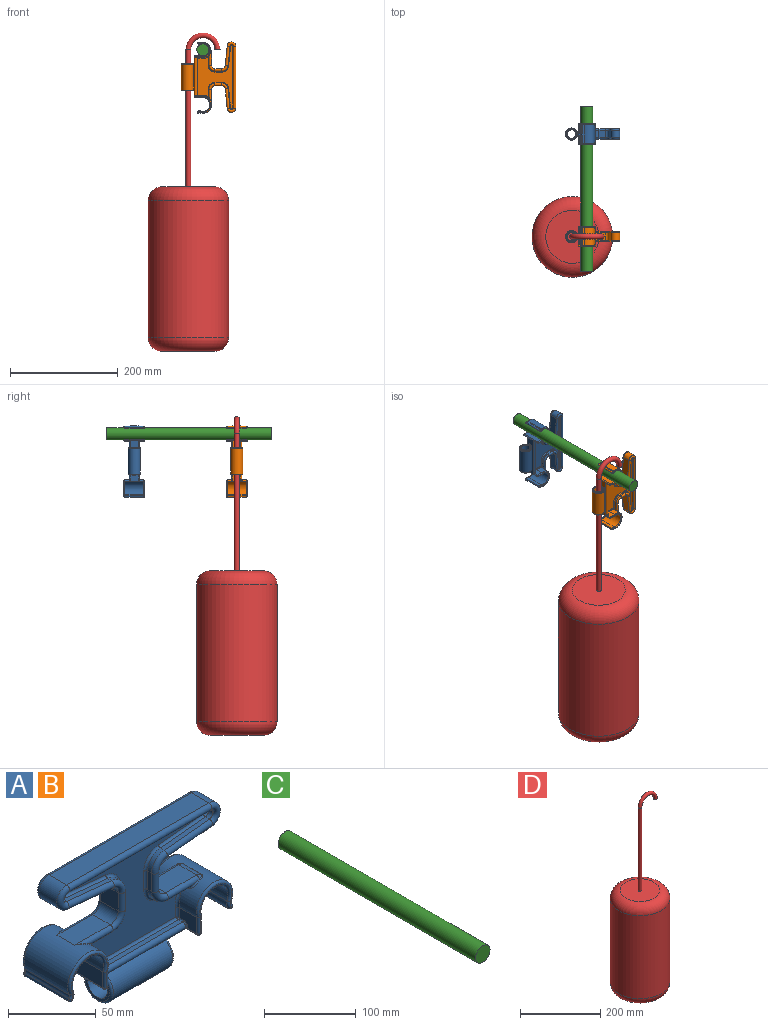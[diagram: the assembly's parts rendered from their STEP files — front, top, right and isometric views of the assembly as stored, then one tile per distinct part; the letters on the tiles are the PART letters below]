
ASSEMBLY  parts=4 mates=3
PART A: 234 faces, bbox 134.5x38.1x102.4 mm
  f0: plane 117.86x64.39mm, normal (0,-1,0), area 2891.2mm2, adj f101,f102,f103,f104,f105,f106,f107,f108
  f1: plane 117.86x64.39mm, normal (0,1,0), area 2891.2mm2, adj f165,f166,f167,f168,f169,f170,f171,f172
  f2: plane 70.47x3.18mm, normal (0,0,1), area 223.7mm2, adj f99,f179,f197,f205
  f3: plane 21.46x19.43mm, normal (1,0,0), area 103.6mm2, adj f69,f219,f228,f229,f230,f231,f232
  f4: plane 21.46x19.43mm, normal (-1,0,0), area 103.6mm2, adj f69,f216,f221,f222,f223,f224,f225
  f5: plane 47.75x0.17mm, normal (0,-1,0), area 8.3mm2, adj f214,f217,f225,f232
  f6: plane 47.75x0.17mm, normal (0,1,0), area 8.3mm2, adj f215,f218,f221,f228
  f7: plane 75.55x35.05mm, normal (0,0,-1), area 753mm2, adj f99,f100,f122,f127,f133,f138,f141,f147
  f8: plane 70.47x3.18mm, normal (0,0,1), area 223.7mm2, adj f100,f112,f201,f211
  f9: plane 17.54x3.18mm, normal (0,0,-1), area 55.7mm2, adj f17,f83,f106,f193
  f10: plane 12.7x3.18mm, normal (-1,0,0), area 40.3mm2, adj f16,f17,f81,f102
  f11: plane 36.31x3.5mm, normal (-0.1,0,1), area 115.8mm2, adj f16,f21,f79,f103
  f12: plane 114.3x3.18mm, normal (0,0,-1), area 362.9mm2, adj f44,f46,f92,f168
  f13: plane 36.31x3.5mm, normal (0.1,0,1), area 115.8mm2, adj f19,f20,f75,f111
  f14: plane 12.7x3.18mm, normal (1,0,0), area 40.3mm2, adj f18,f19,f73,f115
  f15: plane 15.44x3.18mm, normal (0,0,-1), area 49mm2, adj f18,f71,f118,f184
  f16: cylinder r=11.18mm len=11.12mm, axis (0,1,0), area 52.3mm2, adj f10,f11,f80,f101
  f17: cylinder r=11.18mm len=11.18mm, axis (0,1,0), area 55.7mm2, adj f9,f10,f82,f104
  f18: cylinder r=11.18mm len=11.18mm, axis (0,1,0), area 55.7mm2, adj f14,f15,f72,f117
  f19: cylinder r=11.18mm len=11.12mm, axis (0,1,0), area 52.3mm2, adj f13,f14,f74,f113
  f20: cylinder r=3.3mm len=6.59mm, axis (0,1,0), area 31.9mm2, adj f13,f45,f76,f109
  f21: cylinder r=3.3mm len=6.59mm, axis (0,1,0), area 31.9mm2, adj f11,f45,f78,f105
  f22: cylinder r=11.18mm len=11.12mm, axis (0,1,0), area 52.3mm2, adj f23,f47,f89,f174
  f23: plane 12.7x3.18mm, normal (-1,0,0), area 40.3mm2, adj f22,f24,f88,f176
  f24: cylinder r=11.18mm len=11.18mm, axis (0,1,0), area 55.7mm2, adj f23,f25,f87,f178
  f25: plane 17.54x3.18mm, normal (0,0,-1), area 55.7mm2, adj f24,f85,f180,f187
  f26: plane 24.89x14.22mm, normal (0,0,1), area 354mm2, adj f27,f70,f83,f85
  f27: cylinder r=6.35mm len=14.22mm, axis (0,1,0), area 141.9mm2, adj f26,f28,f82,f87
  f28: plane 14.22x12.7mm, normal (1,0,0), area 180.6mm2, adj f27,f29,f81,f88
  f29: cylinder r=6.35mm len=14.22mm, axis (0,1,0), area 133.2mm2, adj f28,f30,f80,f89
  f30: plane 36.31x14.22mm, normal (0.1,0,-1), area 518.9mm2, adj f29,f31,f79,f90
  f31: cylinder r=8.13mm len=16.22mm, axis (0,1,0), area 352.1mm2, adj f30,f32,f78,f91
  f32: plane 114.3x14.22mm, normal (0,0,1), area 1625.8mm2, adj f31,f33,f77,f92
  f33: cylinder r=8.13mm len=16.22mm, axis (0,1,0), area 352.1mm2, adj f32,f34,f76,f93
  f34: plane 36.31x14.22mm, normal (-0.1,0,-1), area 518.9mm2, adj f33,f35,f75,f94
  f35: cylinder r=6.35mm len=14.22mm, axis (0,1,0), area 133.2mm2, adj f34,f36,f74,f95
  f36: plane 14.22x12.7mm, normal (-1,0,0), area 180.6mm2, adj f35,f37,f73,f96
  f37: cylinder r=6.35mm len=14.22mm, axis (0,1,0), area 141.9mm2, adj f36,f38,f72,f97
  f38: plane 28.58x14.22mm, normal (0,0,1), area 406.5mm2, adj f37,f50,f71,f98
  f39: plane 15.44x3.18mm, normal (0,0,-1), area 49mm2, adj f40,f98,f173,f208
  f40: cylinder r=11.18mm len=11.18mm, axis (0,1,0), area 55.7mm2, adj f39,f41,f97,f171
  f41: plane 12.7x3.18mm, normal (1,0,0), area 40.3mm2, adj f40,f42,f96,f169
  f42: cylinder r=11.18mm len=11.12mm, axis (0,1,0), area 52.3mm2, adj f41,f43,f95,f167
  f43: plane 36.31x3.5mm, normal (0.1,0,1), area 115.8mm2, adj f42,f44,f94,f165
  f44: cylinder r=3.3mm len=6.59mm, axis (0,1,0), area 31.9mm2, adj f12,f43,f93,f166
  f45: plane 114.3x3.18mm, normal (0,0,-1), area 362.9mm2, adj f20,f21,f77,f107
  f46: cylinder r=3.3mm len=6.59mm, axis (0,1,0), area 31.9mm2, adj f12,f47,f91,f170
  f47: plane 36.31x3.5mm, normal (-0.1,0,1), area 115.8mm2, adj f22,f46,f90,f172
  f48: plane 13.59x10.78mm, normal (1,0,0), area 122.9mm2, adj f50,f114,f146,f147,f211,f212
  f49: plane 13.59x10.78mm, normal (1,0,0), area 122.9mm2, adj f50,f161,f164,f177,f204,f205
  f50: cylinder r=16mm len=35.05mm, axis (0,1,0), area 1712.8mm2, adj f38,f48,f49,f51,f116,f144,f159,f175
  f51: cylinder r=3.05mm len=35.05mm, axis (0,1,0), area 100.7mm2, adj f50,f52,f142,f156
  f52: cylinder r=1.65mm len=35.05mm, axis (0,1,0), area 181.8mm2, adj f51,f53,f143,f153
  f53: cylinder r=6.35mm len=35.05mm, axis (0,1,0), area 209.8mm2, adj f52,f54,f145,f150
  f54: cylinder r=12.7mm len=35.05mm, axis (0,1,0), area 1670.4mm2, adj f53,f55,f148,f154
  f55: plane 35.05x11.19mm, normal (-1,0,0), area 392.3mm2, adj f54,f151,f157,f158
  f56: plane 28.96x28.96mm, normal (0,-1,0), area 17.6mm2, adj f142,f143,f144,f145,f146,f148,f151,f152
  f57: plane 28.96x28.96mm, normal (0,1,0), area 17.6mm2, adj f150,f153,f154,f156,f157,f159,f161,f162
  f58: plane 13.59x11.2mm, normal (-1,0,0), area 128.5mm2, adj f59,f110,f122,f123,f200,f201
  f59: cylinder r=14.41mm len=35.05mm, axis (0,1,0), area 1533.5mm2, adj f58,f60,f65,f108,f120,f137,f182,f187
  f60: plane 13.59x11.2mm, normal (-1,0,0), area 128.5mm2, adj f59,f139,f141,f181,f196,f197
  f61: plane 35.05x11.6mm, normal (1,0,0), area 406.7mm2, adj f62,f128,f133,f134
  f62: cylinder r=11.11mm len=35.05mm, axis (0,1,0), area 1461.6mm2, adj f61,f63,f126,f131
  f63: cylinder r=6.35mm len=35.05mm, axis (0,1,0), area 209.8mm2, adj f62,f64,f124,f129
  f64: cylinder r=1.65mm len=35.05mm, axis (0,1,0), area 181.8mm2, adj f63,f65,f121,f132
  f65: cylinder r=3.05mm len=35.05mm, axis (0,1,0), area 100.7mm2, adj f59,f64,f119,f135
  f66: plane 27.37x25.78mm, normal (0,-1,0), area 16.2mm2, adj f119,f120,f121,f123,f124,f126,f127,f128
  f67: plane 27.37x25.78mm, normal (0,1,0), area 16.2mm2, adj f129,f131,f132,f134,f135,f137,f138,f139
  f68: cylinder r=11.24mm len=47.75mm, axis (1,0,0), area 3084.8mm2, adj f214,f215,f223,f230
  f69: cylinder r=7.94mm len=50.8mm, axis (1,0,0), area 2533.5mm2, adj f3,f4
  f70: cylinder r=5.08mm len=14.22mm, axis (0,1,0), area 54.6mm2, adj f26,f84,f86,f190
  f71: cylinder r=2.41mm len=28.58mm, axis (-1,0,0), area 151.7mm2, adj f15,f38,f72,f183
  f72: torus R=8.76mm, axis (0,-1,0), area 104.3mm2, adj f18,f37,f71,f73
  f73: cylinder r=2.41mm len=12.7mm, axis (0,0,-1), area 96.3mm2, adj f14,f36,f72,f74
  f74: torus R=8.76mm, axis (0,-1,0), area 98mm2, adj f19,f35,f73,f75
  f75: cylinder r=2.41mm len=36.78mm, axis (1,0,-0.1), area 276.5mm2, adj f13,f34,f74,f76
  f76: torus R=5.71mm, axis (0,-1,0), area 131.9mm2, adj f20,f33,f75,f77
  f77: cylinder r=2.41mm len=114.3mm, axis (-1,0,0), area 866.5mm2, adj f32,f45,f76,f78
  f78: torus R=5.71mm, axis (0,-1,0), area 131.9mm2, adj f21,f31,f77,f79
  f79: cylinder r=2.41mm len=36.78mm, axis (1,0,0.1), area 276.5mm2, adj f11,f30,f78,f80
  f80: torus R=8.76mm, axis (0,-1,0), area 98mm2, adj f16,f29,f79,f81
  f81: cylinder r=2.41mm len=12.7mm, axis (0,0,1), area 96.3mm2, adj f10,f28,f80,f82
  f82: torus R=8.76mm, axis (0,-1,0), area 104.3mm2, adj f17,f27,f81,f83
  f83: cylinder r=2.41mm len=24.89mm, axis (-1,0,0), area 164.4mm2, adj f9,f26,f82,f84,f192
  f84: torus R=2.67mm, axis (0,-1,0), area 7.7mm2, adj f70,f83,f191
  f85: cylinder r=2.41mm len=24.89mm, axis (1,0,0), area 164.4mm2, adj f25,f26,f86,f87,f188
  f86: torus R=2.67mm, axis (0,-1,0), area 7.7mm2, adj f70,f85,f189
  f87: torus R=8.76mm, axis (0,-1,0), area 104.3mm2, adj f24,f27,f85,f88
  f88: cylinder r=2.41mm len=12.7mm, axis (0,0,-1), area 96.3mm2, adj f23,f28,f87,f89
  f89: torus R=8.76mm, axis (0,-1,0), area 98mm2, adj f22,f29,f88,f90
  f90: cylinder r=2.41mm len=36.78mm, axis (-1,0,-0.1), area 276.5mm2, adj f30,f47,f89,f91
  f91: torus R=5.71mm, axis (0,-1,0), area 131.9mm2, adj f31,f46,f90,f92
  f92: cylinder r=2.41mm len=114.3mm, axis (1,0,0), area 866.5mm2, adj f12,f32,f91,f93
  f93: torus R=5.71mm, axis (0,-1,0), area 131.9mm2, adj f33,f44,f92,f94
  f94: cylinder r=2.41mm len=36.78mm, axis (-1,0,0.1), area 276.5mm2, adj f34,f43,f93,f95
  f95: torus R=8.76mm, axis (0,-1,0), area 98mm2, adj f35,f42,f94,f96
  f96: cylinder r=2.41mm len=12.7mm, axis (0,0,1), area 96.3mm2, adj f36,f41,f95,f97
  f97: torus R=8.76mm, axis (0,-1,0), area 104.3mm2, adj f37,f40,f96,f98
  f98: cylinder r=2.41mm len=28.58mm, axis (1,0,0), area 151.7mm2, adj f38,f39,f97,f207
  f99: cylinder r=2.41mm len=75.04mm, axis (-1,0,0), area 539.5mm2, adj f2,f7,f195,f196,f203,f204
  f100: cylinder r=2.41mm len=75.04mm, axis (1,0,0), area 539.5mm2, adj f7,f8,f199,f200,f212,f213
  f101: torus R=12.7mm, axis (0,-1,0), area 41.4mm2, adj f0,f16,f102,f103
  f102: cylinder r=1.52mm len=12.7mm, axis (0,0,-1), area 30.4mm2, adj f0,f10,f101,f104
  f103: cylinder r=1.52mm len=36.46mm, axis (-1,0,-0.1), area 87.3mm2, adj f0,f11,f101,f105
  f104: torus R=12.7mm, axis (0,-1,0), area 44.1mm2, adj f0,f17,f102,f106
  f105: torus R=1.78mm, axis (0,-1,0), area 20mm2, adj f0,f21,f103,f107
  f106: cylinder r=1.52mm len=17.54mm, axis (1,0,0), area 40mm2, adj f0,f9,f104,f194
  f107: cylinder r=1.52mm len=114.3mm, axis (-1,0,0), area 273.6mm2, adj f0,f45,f105,f109
  f108: torus R=15.94mm, axis (0,-1,0), area 33.2mm2, adj f0,f59,f110,f194
  f109: torus R=1.78mm, axis (0,-1,0), area 20mm2, adj f0,f20,f107,f111
  f110: cylinder r=1.52mm len=7.13mm, axis (0,0,-1), area 16mm2, adj f0,f58,f108,f202
  f111: cylinder r=1.52mm len=36.46mm, axis (-1,0,0.1), area 87.3mm2, adj f0,f13,f109,f113
  f112: cylinder r=1.52mm len=70.47mm, axis (1,0,0), area 166.9mm2, adj f0,f8,f202,f210
  f113: torus R=12.7mm, axis (0,-1,0), area 41.4mm2, adj f0,f19,f111,f115
  f114: cylinder r=1.52mm len=6.72mm, axis (0,0,1), area 15mm2, adj f0,f48,f116,f210
  f115: cylinder r=1.52mm len=12.7mm, axis (0,0,1), area 30.4mm2, adj f0,f14,f113,f117
  f116: torus R=17.53mm, axis (0,-1,0), area 33.8mm2, adj f0,f50,f114,f185
  f117: torus R=12.7mm, axis (0,-1,0), area 44.1mm2, adj f0,f18,f115,f118
  f118: cylinder r=1.52mm len=15.44mm, axis (1,0,0), area 35.2mm2, adj f0,f15,f117,f185
  f119: torus R=4.57mm, axis (0,-1,0), area 8.1mm2, adj f65,f66,f120,f121
  f120: torus R=12.89mm, axis (0,-1,0), area 123.7mm2, adj f59,f66,f119,f123
  f121: torus R=0.13mm, axis (0,-1,0), area 8.3mm2, adj f64,f66,f119,f124
  f122: cylinder r=1.52mm len=10.41mm, axis (0,1,0), area 21.3mm2, adj f7,f58,f125,f199
  f123: cylinder r=1.52mm len=11.38mm, axis (0,0,1), area 27mm2, adj f58,f66,f120,f125
  f124: torus R=4.83mm, axis (0,-1,0), area 13.1mm2, adj f63,f66,f121,f126
  f125: sphere r=1.52mm, area 3.6mm2, adj f122,f123,f127
  f126: torus R=12.64mm, axis (0,-1,0), area 104.6mm2, adj f62,f66,f124,f128
  f127: cylinder r=1.52mm len=1.52mm, axis (1,0,0), area 0.6mm2, adj f7,f66,f125,f130
  f128: cylinder r=1.52mm len=11.6mm, axis (0,0,-1), area 27.5mm2, adj f61,f66,f126,f130
  f129: torus R=4.83mm, axis (0,-1,0), area 13.1mm2, adj f63,f67,f131,f132
  f130: sphere r=1.52mm, area 3.6mm2, adj f127,f128,f133
  f131: torus R=12.64mm, axis (0,-1,0), area 104.6mm2, adj f62,f67,f129,f134
  f132: torus R=0.13mm, axis (0,-1,0), area 8.3mm2, adj f64,f67,f129,f135
  f133: cylinder r=1.52mm len=35.05mm, axis (0,-1,0), area 83.9mm2, adj f7,f61,f130,f136
  f134: cylinder r=1.52mm len=11.6mm, axis (0,0,1), area 27.5mm2, adj f61,f67,f131,f136
  f135: torus R=4.57mm, axis (0,-1,0), area 8.1mm2, adj f65,f67,f132,f137
  f136: sphere r=1.52mm, area 3.6mm2, adj f133,f134,f138
  f137: torus R=12.89mm, axis (0,-1,0), area 123.7mm2, adj f59,f67,f135,f139
  f138: cylinder r=1.52mm len=1.52mm, axis (-1,0,0), area 0.6mm2, adj f7,f67,f136,f140
  f139: cylinder r=1.52mm len=11.38mm, axis (0,0,-1), area 27mm2, adj f60,f67,f137,f140
  f140: sphere r=1.52mm, area 3.6mm2, adj f138,f139,f141
  f141: cylinder r=1.52mm len=10.41mm, axis (0,1,0), area 21.3mm2, adj f7,f60,f140,f195
  f142: torus R=4.57mm, axis (0,-1,0), area 8.1mm2, adj f51,f56,f143,f144
  f143: torus R=0.13mm, axis (0,-1,0), area 8.3mm2, adj f52,f56,f142,f145
  f144: torus R=14.48mm, axis (0,-1,0), area 137.9mm2, adj f50,f56,f142,f146
  f145: torus R=4.83mm, axis (0,-1,0), area 13.1mm2, adj f53,f56,f143,f148
  f146: cylinder r=1.52mm len=10.96mm, axis (0,0,-1), area 26mm2, adj f48,f56,f144,f149
  f147: cylinder r=1.52mm len=10.41mm, axis (0,-1,0), area 21.3mm2, adj f7,f48,f149,f213
  f148: torus R=14.22mm, axis (0,-1,0), area 118.8mm2, adj f54,f56,f145,f151
  f149: sphere r=1.52mm, area 3.6mm2, adj f146,f147,f152
  f150: torus R=4.83mm, axis (0,-1,0), area 13.1mm2, adj f53,f57,f153,f154
  f151: cylinder r=1.52mm len=11.19mm, axis (0,0,1), area 26.6mm2, adj f55,f56,f148,f155
  f152: cylinder r=1.52mm len=1.52mm, axis (-1,0,0), area 0.6mm2, adj f7,f56,f149,f155
  f153: torus R=0.13mm, axis (0,-1,0), area 8.3mm2, adj f52,f57,f150,f156
  f154: torus R=14.22mm, axis (0,-1,0), area 118.8mm2, adj f54,f57,f150,f157
  f155: sphere r=1.52mm, area 3.6mm2, adj f151,f152,f158
  f156: torus R=4.57mm, axis (0,-1,0), area 8.1mm2, adj f51,f57,f153,f159
  f157: cylinder r=1.52mm len=11.19mm, axis (0,0,-1), area 26.6mm2, adj f55,f57,f154,f160
  f158: cylinder r=1.52mm len=35.05mm, axis (0,1,0), area 83.9mm2, adj f7,f55,f155,f160
  f159: torus R=14.48mm, axis (0,-1,0), area 137.9mm2, adj f50,f57,f156,f161
  f160: sphere r=1.52mm, area 3.6mm2, adj f157,f158,f162
  f161: cylinder r=1.52mm len=10.96mm, axis (0,0,1), area 26mm2, adj f49,f57,f159,f163
  f162: cylinder r=1.52mm len=1.52mm, axis (1,0,0), area 0.6mm2, adj f7,f57,f160,f163
  f163: sphere r=1.52mm, area 3.6mm2, adj f161,f162,f164
  f164: cylinder r=1.52mm len=10.41mm, axis (0,-1,0), area 21.3mm2, adj f7,f49,f163,f203
  f165: cylinder r=1.52mm len=36.46mm, axis (1,0,-0.1), area 87.3mm2, adj f1,f43,f166,f167
  f166: torus R=1.78mm, axis (0,-1,0), area 20mm2, adj f1,f44,f165,f168
  f167: torus R=12.7mm, axis (0,-1,0), area 41.4mm2, adj f1,f42,f165,f169
  f168: cylinder r=1.52mm len=114.3mm, axis (1,0,0), area 273.6mm2, adj f1,f12,f166,f170
  f169: cylinder r=1.52mm len=12.7mm, axis (0,0,-1), area 30.4mm2, adj f1,f41,f167,f171
  f170: torus R=1.78mm, axis (0,-1,0), area 20mm2, adj f1,f46,f168,f172
  f171: torus R=12.7mm, axis (0,-1,0), area 44.1mm2, adj f1,f40,f169,f173
  f172: cylinder r=1.52mm len=36.46mm, axis (1,0,0.1), area 87.3mm2, adj f1,f47,f170,f174
  f173: cylinder r=1.52mm len=15.44mm, axis (-1,0,0), area 35.2mm2, adj f1,f39,f171,f209
  f174: torus R=12.7mm, axis (0,-1,0), area 41.4mm2, adj f1,f22,f172,f176
  f175: torus R=17.53mm, axis (0,-1,0), area 33.8mm2, adj f1,f50,f177,f209
  f176: cylinder r=1.52mm len=12.7mm, axis (0,0,1), area 30.4mm2, adj f1,f23,f174,f178
  f177: cylinder r=1.52mm len=6.72mm, axis (0,0,-1), area 15mm2, adj f1,f49,f175,f206
  f178: torus R=12.7mm, axis (0,-1,0), area 44.1mm2, adj f1,f24,f176,f180
  f179: cylinder r=1.52mm len=70.47mm, axis (-1,0,0), area 166.9mm2, adj f1,f2,f198,f206
  f180: cylinder r=1.52mm len=17.54mm, axis (-1,0,0), area 40mm2, adj f1,f25,f178,f186
  f181: cylinder r=1.52mm len=7.13mm, axis (0,0,1), area 16mm2, adj f1,f60,f182,f198
  f182: torus R=15.94mm, axis (0,-1,0), area 33.2mm2, adj f1,f59,f181,f186
  f183: bspline ~13.14x6.06mm, area 12.4mm2, adj f50,f71,f184
  f184: cylinder r=0.76mm len=3.18mm, axis (0,1,0), area 5.4mm2, adj f15,f50,f183,f185
  f185: bspline ~3.07x1.9mm, area 3mm2, adj f116,f118,f184
  f186: bspline ~3.41x1.96mm, area 3.2mm2, adj f180,f182,f187
  f187: cylinder r=0.76mm len=3.18mm, axis (0,1,0), area 5.6mm2, adj f25,f59,f186,f188
  f188: bspline ~8.96x4.79mm, area 12.3mm2, adj f59,f85,f187,f189
  f189: bspline ~4.25x3.52mm, area 3.6mm2, adj f59,f86,f188,f190
  f190: cylinder r=0.76mm len=14.22mm, axis (0,-1,0), area 8mm2, adj f59,f70,f189,f191
  f191: bspline ~5.01x3.55mm, area 3.6mm2, adj f59,f84,f190,f192
  f192: bspline ~8.91x4.78mm, area 12.3mm2, adj f59,f83,f191,f193
  f193: cylinder r=0.76mm len=3.18mm, axis (0,1,0), area 5.6mm2, adj f9,f59,f192,f194
  f194: bspline ~3.41x1.96mm, area 3.2mm2, adj f106,f108,f193
  f195: bspline ~3.14x2.29mm, area 1.5mm2, adj f99,f141,f196
  f196: torus R=3.17mm, axis (1,0,0), area 6mm2, adj f60,f99,f195,f197
  f197: cylinder r=0.76mm len=3.18mm, axis (0,-1,0), area 3.8mm2, adj f2,f60,f196,f198
  f198: bspline ~1.6x1.52mm, area 1.9mm2, adj f179,f181,f197
  f199: bspline ~3.14x2.29mm, area 1.5mm2, adj f100,f122,f200
  f200: torus R=3.17mm, axis (1,0,0), area 6mm2, adj f58,f100,f199,f201
  f201: cylinder r=0.76mm len=3.18mm, axis (0,-1,0), area 3.8mm2, adj f8,f58,f200,f202
  f202: bspline ~1.82x1.52mm, area 1.9mm2, adj f110,f112,f201
  f203: bspline ~3.05x2.29mm, area 1.5mm2, adj f99,f164,f204
  f204: torus R=3.17mm, axis (1,0,0), area 6mm2, adj f49,f99,f203,f205
  f205: cylinder r=0.76mm len=3.18mm, axis (0,1,0), area 3.8mm2, adj f2,f49,f204,f206
  f206: bspline ~1.82x1.52mm, area 1.9mm2, adj f177,f179,f205
  f207: bspline ~13.14x6.06mm, area 12.4mm2, adj f50,f98,f208
  f208: cylinder r=0.76mm len=3.18mm, axis (0,1,0), area 5.4mm2, adj f39,f50,f207,f209
  f209: bspline ~3.07x1.9mm, area 3mm2, adj f173,f175,f208
  f210: bspline ~1.6x1.52mm, area 1.9mm2, adj f112,f114,f211
  f211: cylinder r=0.76mm len=3.18mm, axis (0,1,0), area 3.8mm2, adj f8,f48,f210,f212
  f212: torus R=3.17mm, axis (1,0,0), area 6mm2, adj f48,f100,f211,f213
  f213: bspline ~3.05x2.29mm, area 1.5mm2, adj f100,f147,f212
  f214: cylinder r=0.76mm len=47.75mm, axis (1,0,0), area 47.4mm2, adj f5,f68,f224,f231
  f215: cylinder r=0.76mm len=47.75mm, axis (1,0,0), area 47.4mm2, adj f6,f68,f222,f229
  f216: cylinder r=0.76mm len=6.35mm, axis (0,1,0), area 4.1mm2, adj f4,f7,f220,f226
  f217: cylinder r=0.76mm len=52.32mm, axis (-1,0,0), area 59.1mm2, adj f5,f7,f226,f233
  f218: cylinder r=0.76mm len=52.32mm, axis (1,0,0), area 59.1mm2, adj f6,f7,f220,f227
  f219: cylinder r=0.76mm len=6.35mm, axis (0,1,0), area 4.1mm2, adj f3,f7,f227,f233
  f220: bspline ~2.29x2.29mm, area 2.3mm2, adj f216,f218,f221
  f221: cylinder r=1.52mm len=1.52mm, axis (0,0,-1), area 0.4mm2, adj f4,f6,f220,f222
  f222: torus R=2.29mm, axis (-1,0,0), area 4.1mm2, adj f4,f215,f221,f223
  f223: torus R=9.72mm, axis (-1,0,0), area 147mm2, adj f4,f68,f222,f224
  f224: torus R=2.29mm, axis (-1,0,0), area 4.1mm2, adj f4,f214,f223,f225
  f225: cylinder r=1.52mm len=1.52mm, axis (0,0,1), area 0.4mm2, adj f4,f5,f224,f226
  f226: bspline ~2.29x2.29mm, area 2.3mm2, adj f216,f217,f225
  f227: bspline ~2.29x2.29mm, area 2.4mm2, adj f218,f219,f228
  f228: cylinder r=1.52mm len=1.52mm, axis (0,0,1), area 0.4mm2, adj f3,f6,f227,f229
  f229: torus R=2.29mm, axis (1,0,0), area 4.1mm2, adj f3,f215,f228,f230
  f230: torus R=9.72mm, axis (1,0,0), area 147mm2, adj f3,f68,f229,f231
  f231: torus R=2.29mm, axis (1,0,0), area 4.1mm2, adj f3,f214,f230,f232
  f232: cylinder r=1.52mm len=1.52mm, axis (0,0,-1), area 0.4mm2, adj f3,f5,f231,f233
  f233: bspline ~2.29x2.29mm, area 2.4mm2, adj f217,f219,f232
PART B: same geometry as A
PART C: 3 faces, bbox 22.2x304.8x22.2 mm
  f0: cylinder r=11.11mm len=304.8mm, axis (0,1,0), area 21281.7mm2, adj f1,f2
  f1: plane 22.23x22.23mm, normal (0,-1,0), area 387.9mm2, adj f0
  f2: plane 22.23x22.23mm, normal (0,1,0), area 387.9mm2, adj f0
PART D: 8 faces, bbox 161.5x161.5x593.2 mm
  f0: plane 98.43x98.43mm, normal (0,0,1), area 7537.3mm2, adj f1,f6
  f1: torus R=49.21mm, axis (0,0,1), area 16390.6mm2, adj f0,f2
  f2: cylinder r=74.61mm len=254mm, axis (0,0,1), area 119076.3mm2, adj f1,f3
  f3: torus R=49.21mm, axis (0,0,1), area 16390.6mm2, adj f2,f4
  f4: plane 98.43x98.43mm, normal (0,0,-1), area 7608.5mm2, adj f3
  f5: plane 9.53x9.53mm, normal (0,0,-1), area 71.3mm2, adj f7
  f6: cylinder r=4.76mm len=254mm, axis (0,0,1), area 7600.6mm2, adj f0,f7
  f7: torus R=26.99mm, axis (0,1,0), area 2537mm2, adj f5,f6
PLACE A rot(axis=(-0.71,0,-0.71),180deg) t=(2.36,102.63,283.11)mm
PLACE B rot(axis=(-0.71,0,-0.71),180deg) t=(2.36,-87.42,283.11)mm
PLACE C t=(18.36,0.75,333.91)mm
PLACE D t=(-8.63,-87.42,-148.69)mm
MATE slider A.f59 <-> C.f0  axis (0,-1,0) through (18.36,102.63,333.91)mm
MATE slider C.f0 <-> D.f7  axis (0,1,0) through (18.36,0.75,333.91)mm
MATE slider D.f7 <-> B.f59  axis (0,1,0) through (18.36,-87.42,333.91)mm
